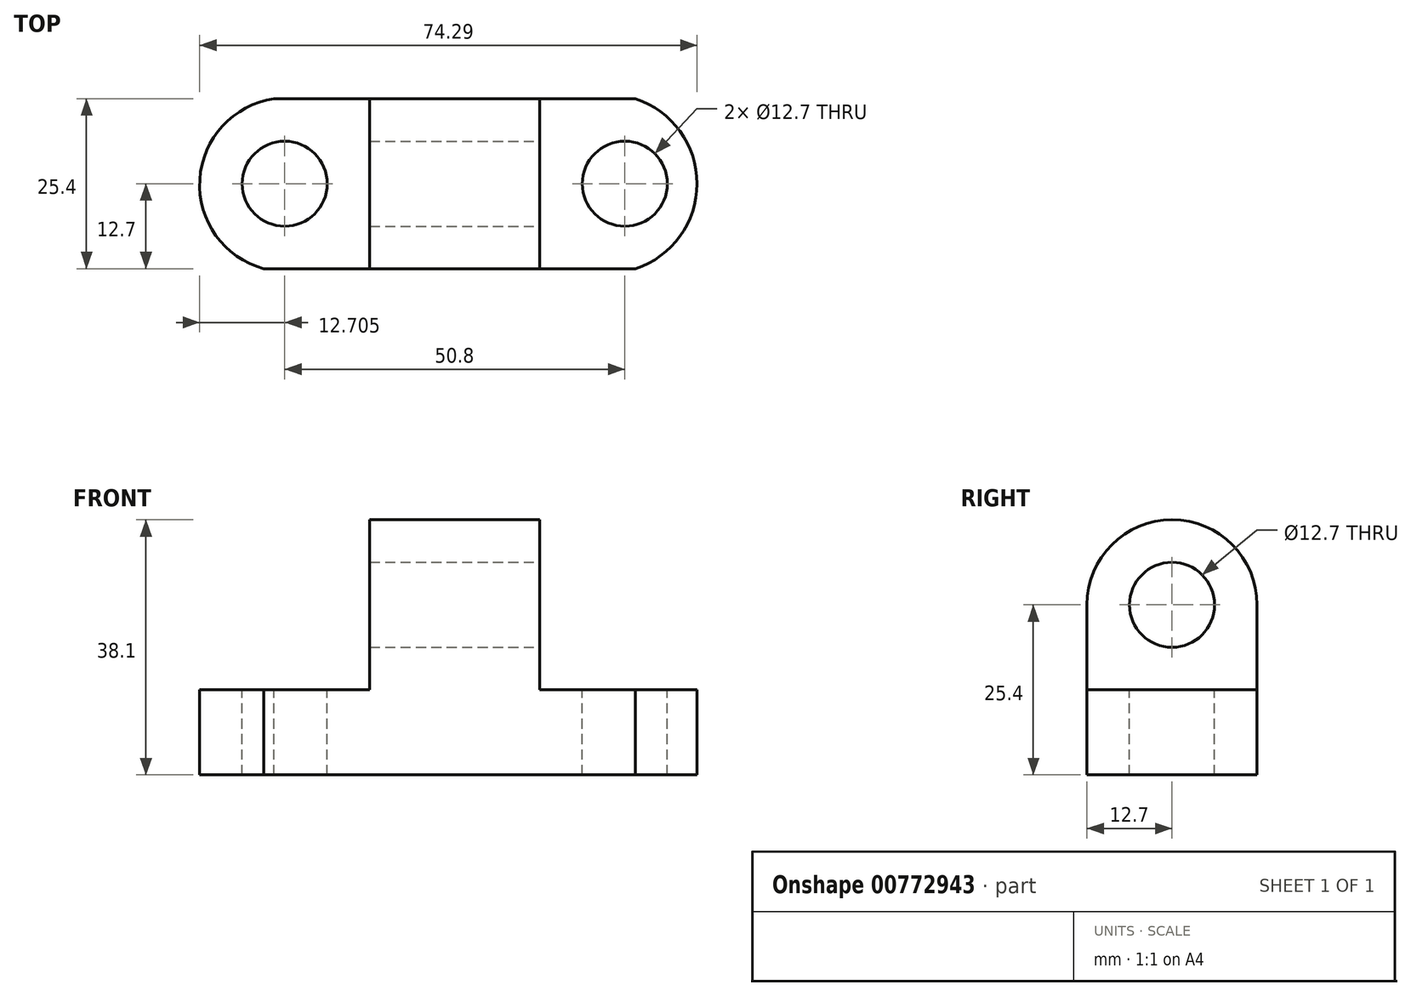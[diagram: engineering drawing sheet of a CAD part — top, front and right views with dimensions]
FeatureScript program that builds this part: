
annotation { "Feature Type Name" : "Feature", "Feature Type Description" : "" }
export const myFeature = defineFeature(function(context is Context, id is Id, definition is map)
    precondition{}
    {
        {
            var Q0;
            Q0=qCreatedBy(makeId("Front.planeOp"),FACE);
            var sketch = newSketch(context, id + "F0", { "sketchPlane" : qUnion([Q0])});
            skLineSegment(sketch, "E0", {"start": v(0, 0) * mm, "end": v(82.55, 0) * mm});
            skLineSegment(sketch, "E1", {"start": v(82.55, 0) * mm, "end": v(82.55, 38.1) * mm});
            skLineSegment(sketch, "E2", {"start": v(82.55, 38.1) * mm, "end": v(0, 38.1) * mm});
            skLineSegment(sketch, "E3", {"start": v(0, 38.1) * mm, "end": v(0, 0) * mm});
            skSolve(sketch);
        }
        {
            var Q0;
            Q0=makeQuery(id+"F0.imprint","IMPRINT",FACE,{"disambiguationData":[TD([[makeQuery(id+"F0.imprint","IMPRINT",EDGE,{"derivedFrom":sQuery(id+"F0.wireOp",EDGE,"E0")}),1.0]])]});
            extrude(context, id + "F1", {"entities" : qUnion([Q0]), "depth" : 25.4 * mm, "offsetDistance" : 25.4 * mm});
        }
        {
            var Q0;
            Q0=makeQuery(id+"F1.opExtrude","CAP_FACE",FACE,{"disambiguationData":[OSD([sQuery(id+"F0.wireOp",EDGE,"E0"),sQuery(id+"F0.wireOp",EDGE,"E1"),sQuery(id+"F0.wireOp",EDGE,"E2"),sQuery(id+"F0.wireOp",EDGE,"E3")])],"isStart":false});
            var sketch = newSketch(context, id + "F2", { "sketchPlane" : qUnion([Q0])});
            skLineSegment(sketch, "E4", {"start": v(0, 12.7) * mm, "end": v(28.57, 12.7) * mm});
            skLineSegment(sketch, "E5", {"start": v(28.57, 12.7) * mm, "end": v(28.57, 38.1) * mm});
            skLineSegment(sketch, "E6", {"start": v(28.57, 38.1) * mm, "end": v(0, 38.1) * mm});
            skLineSegment(sketch, "E7", {"start": v(0, 38.1) * mm, "end": v(0, 12.7) * mm});
            skLineSegment(sketch, "E8", {"start": v(53.98, 38.1) * mm, "end": v(53.98, 12.7) * mm});
            skLineSegment(sketch, "E9", {"start": v(53.98, 12.7) * mm, "end": v(82.55, 12.7) * mm});
            skLineSegment(sketch, "E10", {"start": v(82.55, 12.7) * mm, "end": v(82.55, 38.1) * mm});
            skLineSegment(sketch, "E11", {"start": v(82.55, 38.1) * mm, "end": v(53.98, 38.1) * mm});
            skSolve(sketch);
        }
        {
            var Q0;
            Q0=makeQuery(id+"F2.imprint","IMPRINT",FACE,{"disambiguationData":[TD([[makeQuery(id+"F2.imprint","IMPRINT",EDGE,{"derivedFrom":sQuery(id+"F2.wireOp",EDGE,"E4")}),1.0]])]});
            var Q1;
            Q1=makeQuery(id+"F2.imprint","IMPRINT",FACE,{"disambiguationData":[TD([[makeQuery(id+"F2.imprint","IMPRINT",EDGE,{"derivedFrom":sQuery(id+"F2.wireOp",EDGE,"E8")}),1.0]])]});
            extrude(context, id + "F3", {"entities" : qUnion([Q0, Q1]), "operationType" : NewBodyOperationType.REMOVE, "oppositeDirection" : true, "depth" : 25.4 * mm, "offsetDistance" : 25.4 * mm});
        }
        {
            var Q0;
            Q0=makeQuery(id+"F1.opExtrude","CAP_EDGE",EDGE,{"disambiguationData":[OSD([sQuery(id+"F0.wireOp",EDGE,"E2")])],"isStart":true});
            var Q1;
            Q1=makeQuery(id+"F1.opExtrude","CAP_EDGE",EDGE,{"disambiguationData":[OSD([sQuery(id+"F0.wireOp",EDGE,"E2")])],"isStart":false});
            fillet(context, id + "F4", {"entities" : qUnion([Q0, Q1]), "radius" : 12.7 * mm, "tangentPropagation" : true, "allowEdgeOverflow" : false});
        }
        {
            var Q0;
            Q0=makeQuery(id+"F3.boolean.opBoolean","COPY",FACE,{"derivedFrom":makeQuery(id+"F3.opExtrude","SWEPT_FACE",FACE,{"disambiguationData":[OSD([sQuery(id+"F2.wireOp",EDGE,"E9")])]})});
            var sketch = newSketch(context, id + "F5", { "sketchPlane" : qUnion([Q0])});
            skArc(sketch, "E12", {"start": v(68.26, -25.4) * mm, "mid": v(77.46, -12.7) * mm, "end": v(68.26, 0) * mm});
            skSolve(sketch);
        }
        {
            var Q0;
            {var subQ0=sQuery(id+"F5.wireOp",EDGE,"mobhQzjm-0oRQ-5dLC-3JBl-cufeEKitzcm4");var subQ1=sQuery(id+"F2.wireOp",EDGE,"E9");var subQ2=makeQuery(id+"F3.boolean.opBoolean","COPY",EDGE,{"derivedFrom":makeQuery(id+"F3.opExtrude","CAP_EDGE",EDGE,{"disambiguationData":[OSD([subQ1])],"isStart":false})});var subQ3=makeQuery(id+"F5.imprint","INTERSECT",VERTEX,{"derivedFrom":[subQ2,subQ0]});Q0=makeQuery(id+"F5.imprint","IMPRINT",FACE,{"disambiguationData":[TD([[makeQuery(id+"F5.imprint","IMPRINT",EDGE,{"disambiguationData":[TD([[subQ3,1.0]])],"derivedFrom":subQ0}),-1.0]])]});}
            var Q1;
            {var subQ0=sQuery(id+"F5.wireOp",EDGE,"mobhQzjm-0oRQ-5dLC-3JBl-cufeEKitzcm4");var subQ1=sQuery(id+"F2.wireOp",EDGE,"E9");var subQ2=makeQuery(id+"F3.boolean.opBoolean","COPY",EDGE,{"derivedFrom":makeQuery(id+"F3.opExtrude","CAP_EDGE",EDGE,{"disambiguationData":[OSD([subQ1])],"isStart":true})});var subQ3=makeQuery(id+"F5.imprint","INTERSECT",VERTEX,{"derivedFrom":[subQ2,subQ0]});Q1=makeQuery(id+"F5.imprint","IMPRINT",FACE,{"disambiguationData":[TD([[makeQuery(id+"F5.imprint","IMPRINT",EDGE,{"disambiguationData":[TD([[subQ3,-1.0]])],"derivedFrom":subQ0}),-1.0]])]});}
            var Q2;
            {var subQ0=sQuery(id+"F5.wireOp",EDGE,"E12");Q2=makeQuery(id+"F5.imprint","IMPRINT",FACE,{"disambiguationData":[TD([[makeQuery(id+"F5.imprint","IMPRINT",EDGE,{"derivedFrom":subQ0}),-1.0]])]});}
            extrude(context, id + "F6", {"entities" : qUnion([Q0, Q1, Q2]), "operationType" : NewBodyOperationType.REMOVE, "oppositeDirection" : true, "depth" : 25.4 * mm, "offsetDistance" : 25.4 * mm});
        }
        {
            var Q0;
            Q0=makeQuery(id+"F3.boolean.opBoolean","COPY",FACE,{"derivedFrom":makeQuery(id+"F3.opExtrude","SWEPT_FACE",FACE,{"disambiguationData":[OSD([sQuery(id+"F2.wireOp",EDGE,"E4")])]})});
            var sketch = newSketch(context, id + "F7", { "sketchPlane" : qUnion([Q0])});
            skArc(sketch, "E13", {"start": v(14.29, 0) * mm, "mid": v(3.2, -12.07) * mm, "end": v(12.73, -25.4) * mm});
            skSolve(sketch);
        }
        {
            var Q0;
            {var subQ0=sQuery(id+"F7.wireOp",EDGE,"E13");Q0=makeQuery(id+"F7.imprint","IMPRINT",FACE,{"disambiguationData":[TD([[makeQuery(id+"F7.imprint","IMPRINT",EDGE,{"derivedFrom":subQ0}),-1.0]])]});}
            extrude(context, id + "F8", {"entities" : qUnion([Q0]), "operationType" : NewBodyOperationType.REMOVE, "oppositeDirection" : true, "depth" : 25.4 * mm, "offsetDistance" : 25.4 * mm});
        }
        {
            var Q0;
            Q0=makeQuery(id+"F3.boolean.opBoolean","COPY",FACE,{"derivedFrom":makeQuery(id+"F3.opExtrude","SWEPT_FACE",FACE,{"disambiguationData":[OSD([sQuery(id+"F2.wireOp",EDGE,"E9")])]})});
            var sketch = newSketch(context, id + "F9", { "sketchPlane" : qUnion([Q0])});
            skCircle(sketch, "E14", {"center": v(66.68, -12.7) * mm, "radius": 6.35 * mm});
            skSolve(sketch);
        }
        {
            var Q0;
            Q0=makeQuery(id+"F9.imprint","IMPRINT",FACE,{"disambiguationData":[TD([[makeQuery(id+"F9.imprint","IMPRINT",EDGE,{"derivedFrom":sQuery(id+"F9.wireOp",EDGE,"E14")}),1.0]])]});
            extrude(context, id + "F10", {"entities" : qUnion([Q0]), "operationType" : NewBodyOperationType.REMOVE, "oppositeDirection" : true, "depth" : 25.4 * mm, "offsetDistance" : 25.4 * mm});
        }
        {
            var Q0;
            Q0=makeQuery(id+"F3.boolean.opBoolean","COPY",FACE,{"derivedFrom":makeQuery(id+"F3.opExtrude","SWEPT_FACE",FACE,{"disambiguationData":[OSD([sQuery(id+"F2.wireOp",EDGE,"E4")])]})});
            var sketch = newSketch(context, id + "F11", { "sketchPlane" : qUnion([Q0])});
            skCircle(sketch, "E15", {"center": v(15.87, -12.7) * mm, "radius": 6.35 * mm});
            skSolve(sketch);
        }
        {
            var Q0;
            Q0=makeQuery(id+"F11.imprint","IMPRINT",FACE,{"disambiguationData":[TD([[makeQuery(id+"F11.imprint","IMPRINT",EDGE,{"derivedFrom":sQuery(id+"F11.wireOp",EDGE,"E15")}),1.0]])]});
            extrude(context, id + "F12", {"entities" : qUnion([Q0]), "operationType" : NewBodyOperationType.REMOVE, "oppositeDirection" : true, "depth" : 25.4 * mm, "offsetDistance" : 25.4 * mm});
        }
        {
            var Q0;
            Q0=makeQuery(id+"F3.boolean.opBoolean","COPY",FACE,{"derivedFrom":makeQuery(id+"F3.opExtrude","SWEPT_FACE",FACE,{"disambiguationData":[OSD([sQuery(id+"F2.wireOp",EDGE,"E8")])]})});
            var sketch = newSketch(context, id + "F13", { "sketchPlane" : qUnion([Q0])});
            skCircle(sketch, "E16", {"center": v(-12.7, 25.4) * mm, "radius": 6.35 * mm});
            skSolve(sketch);
        }
        {
            var Q0;
            Q0=makeQuery(id+"F13.imprint","IMPRINT",FACE,{"disambiguationData":[TD([[makeQuery(id+"F13.imprint","IMPRINT",EDGE,{"derivedFrom":sQuery(id+"F13.wireOp",EDGE,"E16")}),1.0]])]});
            extrude(context, id + "F14", {"entities" : qUnion([Q0]), "operationType" : NewBodyOperationType.REMOVE, "oppositeDirection" : true, "depth" : 25.4 * mm, "offsetDistance" : 25.4 * mm});
        }
    });
